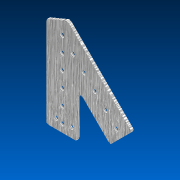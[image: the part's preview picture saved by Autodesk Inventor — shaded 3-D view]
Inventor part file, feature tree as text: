
AUTODESK INVENTOR PART (.ipt)
format: ipt  version: 2022.2 (Build 262287000, 287)  size: 148,992 bytes
history: native  units: in
note: dims shown in document units (in); Inventor stores cm internally (conversion verified against a paired STEP export)
features: other x4, reference x2, extrude x1, sketch x1
ambient origin geometry x8: Origin, YZ Plane, XZ Plane, XY Plane, X Axis, Y Axis, Z Axis, Center Point
bodies: Solid1 (feature_tree)
feature tree (8):
  extrude  "Extrusion1"  [1 undecoded]
  sketch  "Sketch1"  dims[d0=0.0in d1=0.0in]
  reference  "Reference1"
  reference  "Reference2"
  other  "Cut-Extrude2"
  parser-record x1  (decoder bookkeeping rows leaked as tree rows — omitted from the tree; the rows remain in map.json)
  other  "Chassis.iam"
  other  "VersaFrame 135 Degree Gusset Modifed 2(217-3556):1"
note: 1 required parameter value undecoded (feature->parameter linkage not recoverable at this tier; creation-order binding heuristic only, values carry confidence <= 0.55)
note: 1 file-system path scrubbed to <path> (originals preserved in map.json)
